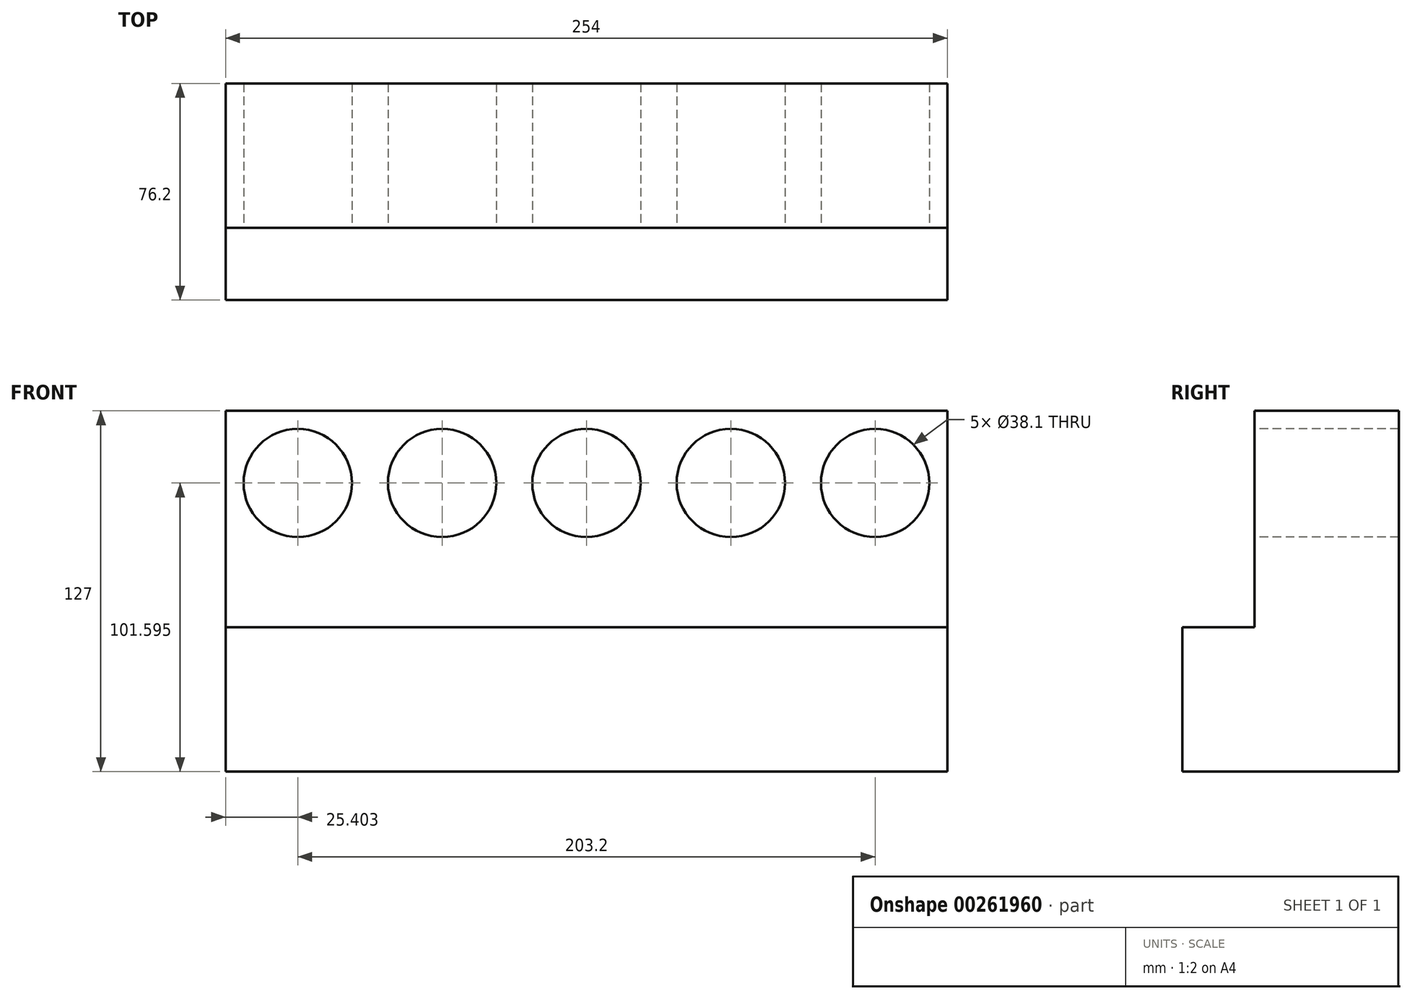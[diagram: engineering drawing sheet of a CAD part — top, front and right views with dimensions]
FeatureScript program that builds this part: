
annotation { "Feature Type Name" : "Feature", "Feature Type Description" : "" }
export const myFeature = defineFeature(function(context is Context, id is Id, definition is map)
    precondition{}
    {
        {
            var Q0;
            Q0=qCreatedBy(makeId("Front.planeOp"),FACE);
            var sketch = newSketch(context, id + "F0", { "sketchPlane" : qUnion([Q0])});
            skLineSegment(sketch, "E0.bottom", {"start": v(-129.32, 45.5) * mm, "end": v(124.68, 45.5) * mm});
            skLineSegment(sketch, "E0.top", {"start": v(-129.32, -81.5) * mm, "end": v(124.68, -81.5) * mm});
            skLineSegment(sketch, "E0.left", {"start": v(-129.32, 45.5) * mm, "end": v(-129.32, -81.5) * mm});
            skLineSegment(sketch, "E0.right", {"start": v(124.68, 45.5) * mm, "end": v(124.68, -81.5) * mm});
            skSolve(sketch);
        }
        {
            var Q0;
            Q0=makeQuery(id+"F0.imprint","IMPRINT",FACE,{"disambiguationData":[TD([[makeQuery(id+"F0.imprint","IMPRINT",EDGE,{"derivedFrom":sQuery(id+"F0.wireOp",EDGE,"E0.bottom")}),-1.0]])]});
            extrude(context, id + "F1", {"entities" : qUnion([Q0]), "depth" : 76.2 * mm});
        }
        {
            var Q0;
            Q0=makeQuery(id+"F1.opExtrude","SWEPT_FACE",FACE,{"disambiguationData":[OSD([sQuery(id+"F0.wireOp",EDGE,"E0.right")])]});
            var sketch = newSketch(context, id + "F2", { "sketchPlane" : qUnion([Q0])});
            skLineSegment(sketch, "E1.bottom", {"start": v(-76.2, 45.5) * mm, "end": v(-50.8, 45.5) * mm});
            skLineSegment(sketch, "E1.top", {"start": v(-76.2, -30.7) * mm, "end": v(-50.8, -30.7) * mm});
            skLineSegment(sketch, "E1.left", {"start": v(-76.2, 45.5) * mm, "end": v(-76.2, -30.7) * mm});
            skLineSegment(sketch, "E1.right", {"start": v(-50.8, 45.5) * mm, "end": v(-50.8, -30.7) * mm});
            skSolve(sketch);
        }
        {
            var Q0;
            Q0=makeQuery(id+"F2.imprint","IMPRINT",FACE,{"disambiguationData":[TD([[makeQuery(id+"F2.imprint","IMPRINT",EDGE,{"derivedFrom":sQuery(id+"F2.wireOp",EDGE,"E1.bottom")}),-1.0]])]});
            extrude(context, id + "F3", {"entities" : qUnion([Q0]), "operationType" : NewBodyOperationType.REMOVE, "oppositeDirection" : true, "depth" : 255.78 * mm});
        }
        {
            var Q0;
            Q0=makeQuery(id+"F3.boolean.opBoolean","COPY",FACE,{"derivedFrom":makeQuery(id+"F3.opExtrude","SWEPT_FACE",FACE,{"disambiguationData":[OSD([sQuery(id+"F2.wireOp",EDGE,"E1.right")])]})});
            var sketch = newSketch(context, id + "F4", { "sketchPlane" : qUnion([Q0])});
            skPoint(sketch, "E2", {"position": v(-103.92, 20.1) * mm});
            skPoint(sketch, "E3", {"position": v(-53.12, 20.1) * mm});
            skPoint(sketch, "E4", {"position": v(-2.32, 20.1) * mm});
            skPoint(sketch, "E5", {"position": v(48.48, 20.1) * mm});
            skPoint(sketch, "E6", {"position": v(99.28, 20.1) * mm});
            skSolve(sketch);
        }
        {
            var Q0;
            Q0=sQuery(id+"F4.wireOp",VERTEX,"E2");
            var Q1;
            Q1=makeQuery(id+"F1.opExtrude","SWEPT_BODY",BODY,{"disambiguationData":[OSD([sQuery(id+"F0.wireOp",EDGE,"E0.bottom"),sQuery(id+"F0.wireOp",EDGE,"E0.top"),sQuery(id+"F0.wireOp",EDGE,"E0.left"),sQuery(id+"F0.wireOp",EDGE,"E0.right")])]});
            hole(context, id + "F5", {"style" : HoleStyle.SIMPLE, "endStyle" : HoleEndStyle.THROUGH, "holeDiameter" : 38.1 * mm, "tappedDepth" : 12.7 * mm, "tapClearance" : 3, "locations" : qUnion([Q0]), "scope" : qUnion([Q1])});
        }
        {
            var Q0;
            Q0=sQuery(id+"F4.wireOp",VERTEX,"E3");
            var Q1;
            Q1=makeQuery(id+"F1.opExtrude","SWEPT_BODY",BODY,{"disambiguationData":[OSD([sQuery(id+"F0.wireOp",EDGE,"E0.bottom"),sQuery(id+"F0.wireOp",EDGE,"E0.top"),sQuery(id+"F0.wireOp",EDGE,"E0.left"),sQuery(id+"F0.wireOp",EDGE,"E0.right")])]});
            hole(context, id + "F6", {"style" : HoleStyle.SIMPLE, "endStyle" : HoleEndStyle.THROUGH, "holeDiameter" : 38.1 * mm, "tappedDepth" : 12.7 * mm, "tapClearance" : 3, "locations" : qUnion([Q0]), "scope" : qUnion([Q1])});
        }
        {
            var Q0;
            Q0=sQuery(id+"F4.wireOp",VERTEX,"E4");
            var Q1;
            Q1=sQuery(id+"F4.wireOp",VERTEX,"E5");
            var Q2;
            Q2=sQuery(id+"F4.wireOp",VERTEX,"E6");
            var Q3;
            Q3=makeQuery(id+"F1.opExtrude","SWEPT_BODY",BODY,{"disambiguationData":[OSD([sQuery(id+"F0.wireOp",EDGE,"E0.bottom"),sQuery(id+"F0.wireOp",EDGE,"E0.top"),sQuery(id+"F0.wireOp",EDGE,"E0.left"),sQuery(id+"F0.wireOp",EDGE,"E0.right")])]});
            hole(context, id + "F7", {"style" : HoleStyle.SIMPLE, "endStyle" : HoleEndStyle.THROUGH, "holeDiameter" : 38.1 * mm, "tappedDepth" : 12.7 * mm, "tapClearance" : 3, "locations" : qUnion([Q0, Q1, Q2]), "scope" : qUnion([Q3])});
        }
    });
